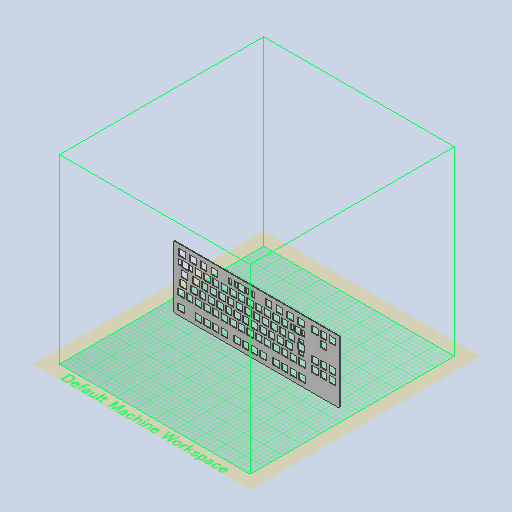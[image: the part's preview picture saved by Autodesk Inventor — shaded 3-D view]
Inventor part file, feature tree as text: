
AUTODESK INVENTOR PART (.ipt)
format: ipt  version: 2022 (Build 260153000, 153)  size: 3,551,232 bytes
history: native  units: mm
features: sketch x22, hole x15, extrude x8, fillet x3, other x1, chamfer x1
ambient origin geometry x8: Origin, YZ Plane, XZ Plane, XY Plane, X Axis, Y Axis, Z Axis, Center Point
bodies: Body1 (feature_tree)
feature tree (50):
  other  "ソリッド1"
  extrude  "押し出し1"  Depth=3.46mm
  extrude  "押し出し2"  Depth=13.9954mm
  extrude  "押し出し3"  Depth=13.9954mm
  extrude  "押し出し4"  Depth=0.254mm
  extrude  "押し出し5"  Depth=19.05mm
  hole  "穴1"  [1 undecoded]
  sketch  "スケッチ10"
  sketch  "スケッチ11"
  sketch  "スケッチ12"
  sketch  "スケッチ13"
  sketch  "スケッチ14"
  sketch  "スケッチ15"
  sketch  "スケッチ16"
  sketch  "スケッチ17"
  sketch  "スケッチ18"
  sketch  "スケッチ19"
  sketch  "スケッチ20"
  sketch  "スケッチ21"
  sketch  "スケッチ22"
  hole  "穴2"  [1 undecoded]
  hole  "穴3"  [1 undecoded]
  hole  "穴4"  [1 undecoded]
  hole  "穴5"  [1 undecoded]
  hole  "穴6"  [1 undecoded]
  hole  "穴7"  [1 undecoded]
  hole  "穴8"  [1 undecoded]
  hole  "穴9"  [1 undecoded]
  hole  "穴10"  [1 undecoded]
  hole  "穴11"  [1 undecoded]
  hole  "穴12"  [1 undecoded]
  hole  "穴13"  [1 undecoded]
  hole  "穴14"  [1 undecoded]
  hole  "穴15"  [1 undecoded]
  fillet  "フィレット6"  Radius=19.05mm
  extrude  "押し出し8"  Depth=13.9954mm TaperAngle=0.0deg
  extrude  "押し出し9"  Depth=21.2725mm
  fillet  "フィレット9"  Radius=13.9954mm
  chamfer  "面取り4"  Distance=110.0mm
  extrude  "押し出し11"  Depth=54.61mm
  fillet  "フィレット10"  Radius=19.05mm
  sketch  "スケッチ2"
  sketch  "スケッチ3"
  sketch  "スケッチ4"
  sketch  "スケッチ5"
  sketch  "スケッチ6"
  sketch  "スケッチ23"
  sketch  "スケッチ26"
  sketch  "スケッチ27"
  sketch  "スケッチ29"
note: 15 required parameter values undecoded (feature->parameter linkage not recoverable at this tier; creation-order binding heuristic only, values carry confidence <= 0.55)
